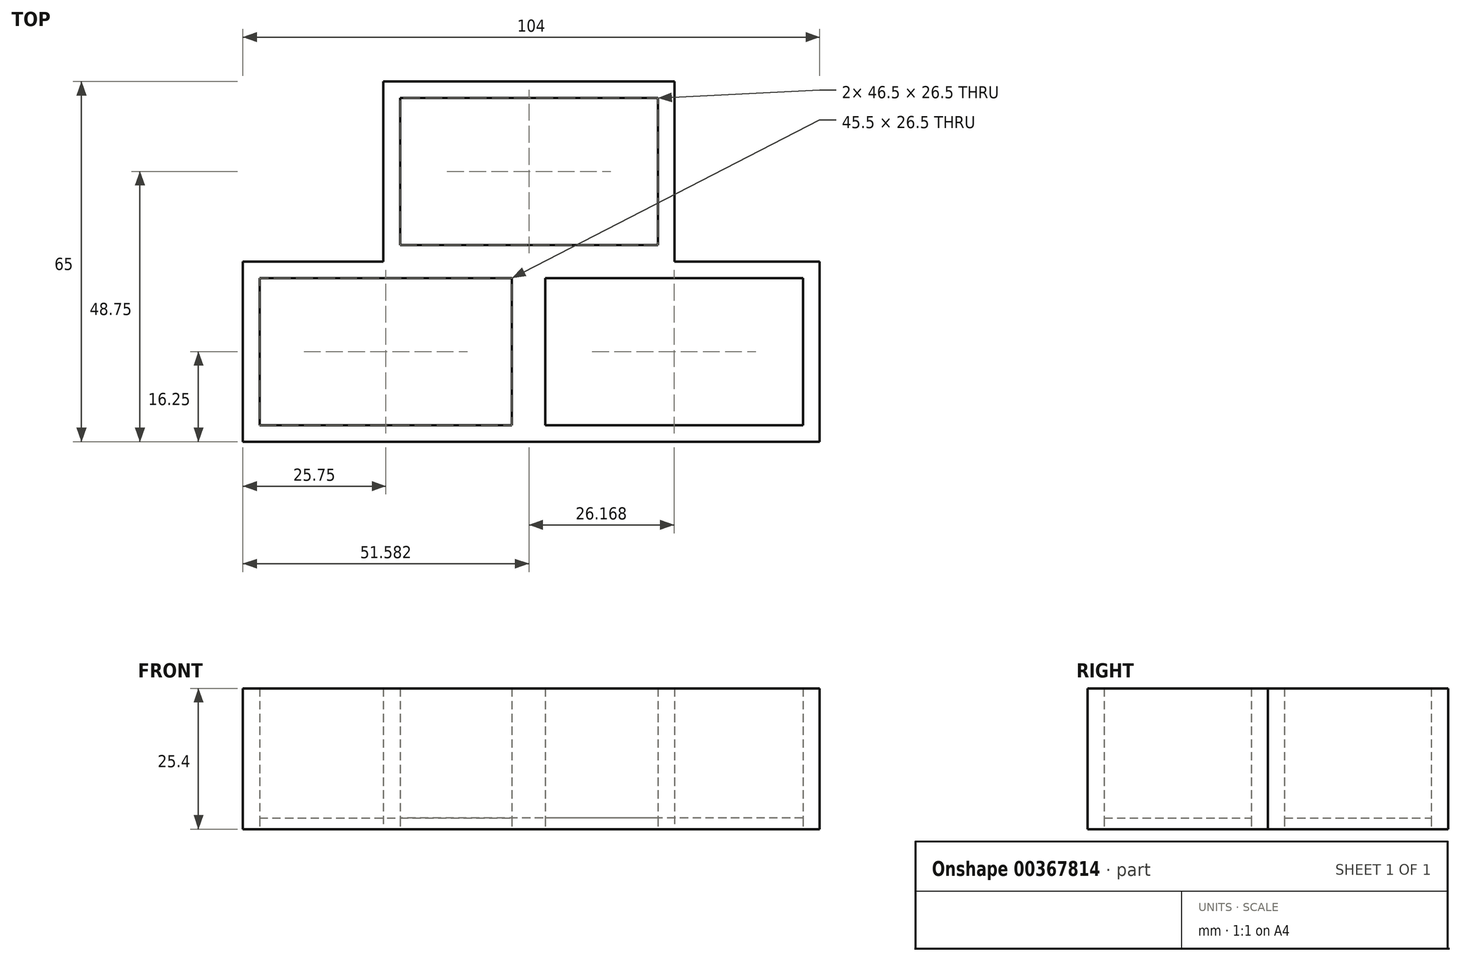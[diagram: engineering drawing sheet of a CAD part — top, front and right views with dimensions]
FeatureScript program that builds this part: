
annotation { "Feature Type Name" : "Feature", "Feature Type Description" : "" }
export const myFeature = defineFeature(function(context is Context, id is Id, definition is map)
    precondition{}
    {
        {
            var Q0;
            Q0=qCreatedBy(makeId("Top.planeOp"),FACE);
            var sketch = newSketch(context, id + "F0", { "sketchPlane" : qUnion([Q0])});
            skLineSegment(sketch, "E0", {"start": v(0.08, 62) * mm, "end": v(26.33, 62) * mm});
            skLineSegment(sketch, "E1", {"start": v(26.33, 62) * mm, "end": v(26.33, 32.5) * mm});
            skLineSegment(sketch, "E2", {"start": v(23.33, 32.5) * mm, "end": v(-23.17, 32.5) * mm});
            skLineSegment(sketch, "E3", {"start": v(-26.17, 32.5) * mm, "end": v(-26.17, 62) * mm});
            skLineSegment(sketch, "E4", {"start": v(0.08, 62) * mm, "end": v(-26.17, 62) * mm});
            skLineSegment(sketch, "E5", {"start": v(3, 0) * mm, "end": v(3, 26.5) * mm});
            skLineSegment(sketch, "E6", {"start": v(3, 26.5) * mm, "end": v(49.5, 26.5) * mm});
            skLineSegment(sketch, "E7", {"start": v(49.5, 26.5) * mm, "end": v(49.5, 0) * mm});
            skLineSegment(sketch, "E8", {"start": v(49.5, 0) * mm, "end": v(3, 0) * mm});
            skLineSegment(sketch, "E9", {"start": v(-3, 0) * mm, "end": v(-3, 26.5) * mm});
            skLineSegment(sketch, "E10", {"start": v(-3, 26.5) * mm, "end": v(-48.5, 26.5) * mm});
            skLineSegment(sketch, "E11", {"start": v(-48.5, 26.5) * mm, "end": v(-48.5, 0) * mm});
            skLineSegment(sketch, "E12", {"start": v(-48.5, 0) * mm, "end": v(-3, 0) * mm});
            skLineSegment(sketch, "E13", {"start": v(-51.5, 26.5) * mm, "end": v(-51.5, 29.5) * mm});
            skLineSegment(sketch, "E14", {"start": v(-51.5, 29.5) * mm, "end": v(-51.5, -3) * mm});
            skLineSegment(sketch, "E15", {"start": v(-48.5, -3) * mm, "end": v(-51.5, -3) * mm});
            skLineSegment(sketch, "E16", {"start": v(-51.5, -3) * mm, "end": v(52.5, -3) * mm});
            skLineSegment(sketch, "E17", {"start": v(52.5, 0) * mm, "end": v(52.5, -3) * mm});
            skLineSegment(sketch, "E18", {"start": v(52.5, -3) * mm, "end": v(52.5, 29.5) * mm});
            skLineSegment(sketch, "E19", {"start": v(-26.17, 32.5) * mm, "end": v(-26.17, 29.5) * mm});
            skLineSegment(sketch, "E20", {"start": v(-26.17, 29.5) * mm, "end": v(-51.5, 29.5) * mm});
            skLineSegment(sketch, "E21", {"start": v(-51.5, 29.5) * mm, "end": v(-26.17, 29.5) * mm});
            skLineSegment(sketch, "E22", {"start": v(26.33, 32.5) * mm, "end": v(26.33, 29.5) * mm});
            skLineSegment(sketch, "E23", {"start": v(-26.17, 62) * mm, "end": v(-23.17, 62) * mm});
            skLineSegment(sketch, "E24", {"start": v(-23.17, 59) * mm, "end": v(-23.17, 32.5) * mm});
            skLineSegment(sketch, "E25", {"start": v(23.33, 32.5) * mm, "end": v(23.33, 59) * mm});
            skLineSegment(sketch, "E26", {"start": v(23.33, 59) * mm, "end": v(-23.17, 59) * mm});
            skLineSegment(sketch, "E27.trimOffspring", {"start": v(26.33, 29.5) * mm, "end": v(52.5, 29.5) * mm});
            skSolve(sketch);
        }
        {
            var Q0;
            Q0=makeQuery(id+"F0.imprint","IMPRINT",FACE,{"disambiguationData":[TD([[makeQuery(id+"F0.imprint","IMPRINT",EDGE,{"derivedFrom":sQuery(id+"F0.wireOp",EDGE,"E9")}),1.0]])]});
            var Q1;
            Q1=makeQuery(id+"F0.imprint","IMPRINT",FACE,{"disambiguationData":[TD([[makeQuery(id+"F0.imprint","IMPRINT",EDGE,{"derivedFrom":sQuery(id+"F0.wireOp",EDGE,"E5")}),-1.0]])]});
            var Q2;
            Q2=makeQuery(id+"F0.imprint","IMPRINT",FACE,{"disambiguationData":[TD([[makeQuery(id+"F0.imprint","IMPRINT",EDGE,{"derivedFrom":sQuery(id+"F0.wireOp",EDGE,"E2")}),-1.0]])]});
            extrude(context, id + "F1", {"entities" : qUnion([Q0, Q1, Q2]), "depth" : 2 * mm});
        }
        {
            var Q0;
            Q0 = qSketchRegion(id + "F0", true);
            extrude(context, id + "F2", {"entities" : qUnion([Q0]), "depth" : 25.4 * mm});
        }
    });
